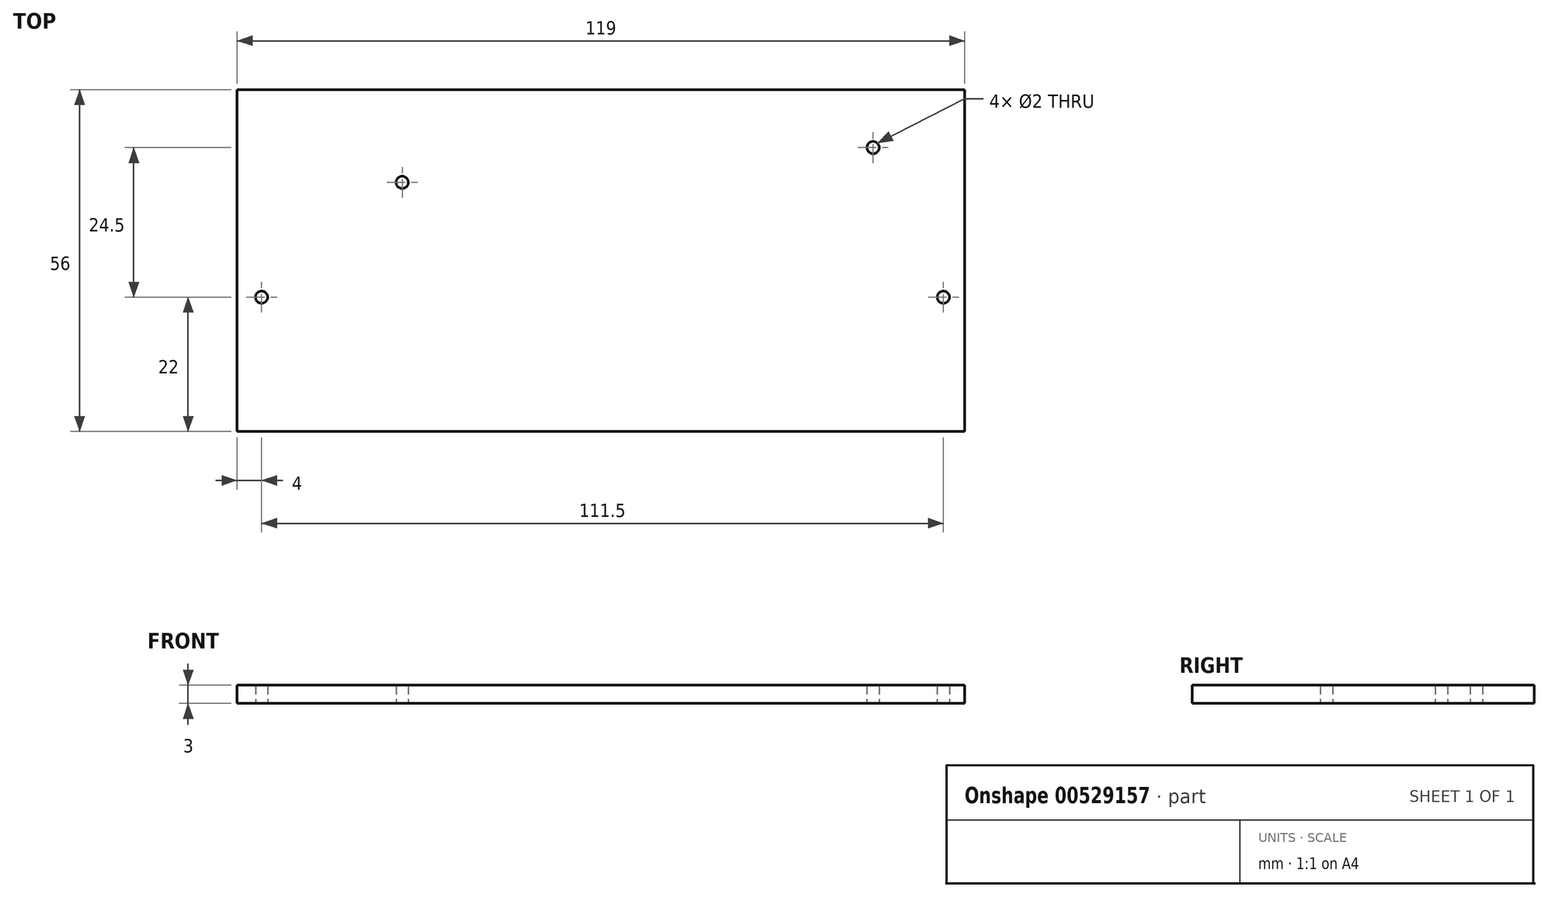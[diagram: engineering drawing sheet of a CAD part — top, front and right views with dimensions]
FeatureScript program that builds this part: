
annotation { "Feature Type Name" : "Feature", "Feature Type Description" : "" }
export const myFeature = defineFeature(function(context is Context, id is Id, definition is map)
    precondition{}
    {
        {
            var Q0;
            Q0=qCreatedBy(makeId("Top.planeOp"),FACE);
            var sketch = newSketch(context, id + "F0", { "sketchPlane" : qUnion([Q0])});
            skLineSegment(sketch, "E0.bottom", {"start": v(59.5, -28) * mm, "end": v(-59.5, -28) * mm});
            skLineSegment(sketch, "E0.top", {"start": v(59.5, 28) * mm, "end": v(-59.5, 28) * mm});
            skLineSegment(sketch, "E0.left", {"start": v(59.5, -28) * mm, "end": v(59.5, 28) * mm});
            skLineSegment(sketch, "E0.right", {"start": v(-59.5, -28) * mm, "end": v(-59.5, 28) * mm});
            skPoint(sketch, "E0.middle", {"position": v(0, 0) * mm});
            skLineSegment(sketch, "E1", {"start": v(-65.34, -6) * mm, "end": v(65.03, -6) * mm, "construction": true});
            skLineSegment(sketch, "E2", {"start": v(-55.5, 30.35) * mm, "end": v(-55.5, -32.52) * mm, "construction": true});
            skCircle(sketch, "E3", {"center": v(-55.5, -6) * mm, "radius": 1 * mm});
            skLineSegment(sketch, "E4", {"start": v(0, 31.84) * mm, "end": v(0, -33.62) * mm, "construction": true});
            skPoint(sketch, "E4.startSnap0", {"position": v(0, 28) * mm});
            skLineSegment(sketch, "E5", {"start": v(-54.5, -6) * mm, "end": v(-54.5, -3.66) * mm, "construction": true});
            skLineSegment(sketch, "E6", {"start": v(-54.5, -3.66) * mm, "end": v(-54.5, -8.09) * mm, "construction": true});
            skLineSegment(sketch, "E7.MirrorCS", {"start": v(55, -3.66) * mm, "end": v(55, -8.09) * mm, "construction": true});
            skLineSegment(sketch, "E8", {"start": v(56, -5.03) * mm, "end": v(56, -7.06) * mm, "construction": true});
            skCircle(sketch, "E9", {"center": v(56, -6) * mm, "radius": 1 * mm});
            skLineSegment(sketch, "E10", {"start": v(57, -6) * mm, "end": v(57, -5.52) * mm, "construction": true});
            skLineSegment(sketch, "E11", {"start": v(57, -5.52) * mm, "end": v(57, -8.56) * mm, "construction": true});
            skLineSegment(sketch, "E12", {"start": v(-56.5, -6) * mm, "end": v(-56.5, -5.18) * mm, "construction": true});
            skLineSegment(sketch, "E13", {"start": v(-56.5, -5.18) * mm, "end": v(-56.5, -8.95) * mm, "construction": true});
            skLineSegment(sketch, "E14", {"start": v(-55.5, -7) * mm, "end": v(-58.27, -7) * mm, "construction": true});
            skLineSegment(sketch, "E15", {"start": v(-58.27, -7) * mm, "end": v(-52.18, -7) * mm, "construction": true});
            skLineSegment(sketch, "E16", {"start": v(-33.5, 31.32) * mm, "end": v(-33.5, -35.04) * mm, "construction": true});
            skLineSegment(sketch, "E17", {"start": v(-68.2, 13.8) * mm, "end": v(-15.57, 13.8) * mm, "construction": true});
            skCircle(sketch, "E18", {"center": v(-32.5, 12.8) * mm, "radius": 1 * mm});
            skLineSegment(sketch, "E19", {"start": v(45.5, 32.36) * mm, "end": v(45.5, -34.55) * mm, "construction": true});
            skLineSegment(sketch, "E20", {"start": v(62.23, 19.5) * mm, "end": v(38.11, 19.5) * mm, "construction": true});
            skCircle(sketch, "E21", {"center": v(44.5, 18.5) * mm, "radius": 1 * mm});
            skSolve(sketch);
        }
        {
            var Q0;
            Q0=makeQuery(id+"F0.imprint","IMPRINT",FACE,{"disambiguationData":[TD([[makeQuery(id+"F0.imprint","IMPRINT",EDGE,{"derivedFrom":sQuery(id+"F0.wireOp",EDGE,"E0.bottom")}),-1.0]])]});
            extrude(context, id + "F1", {"entities" : qUnion([Q0]), "depth" : 3 * mm, "offsetDistance" : 25 * mm});
        }
    });
